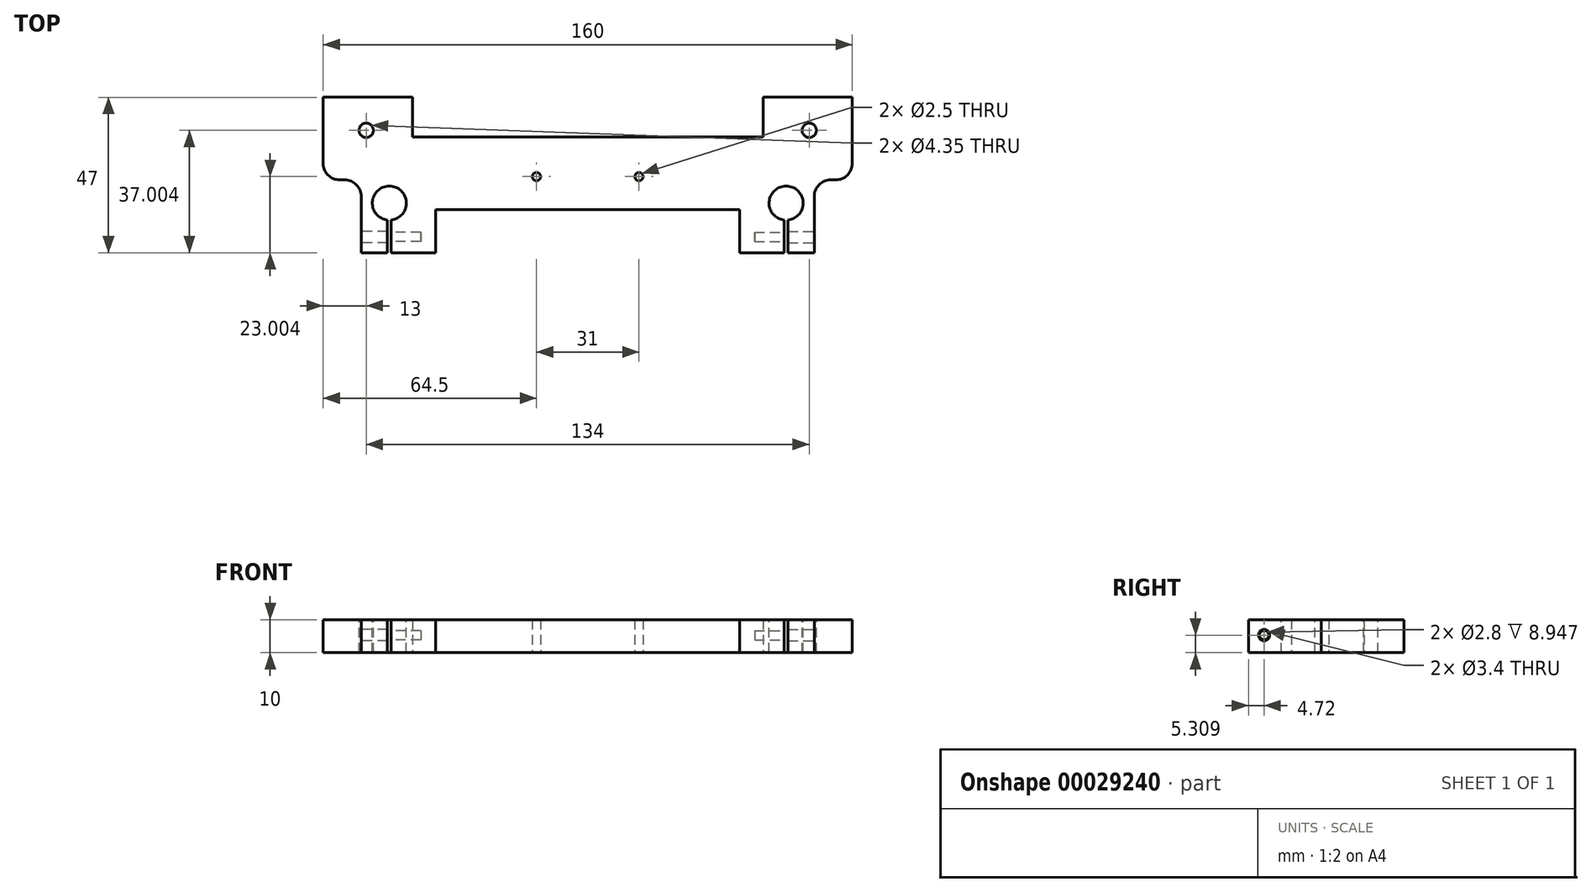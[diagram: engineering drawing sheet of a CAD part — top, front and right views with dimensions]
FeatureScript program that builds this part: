
annotation { "Feature Type Name" : "Feature", "Feature Type Description" : "" }
export const myFeature = defineFeature(function(context is Context, id is Id, definition is map)
    precondition{}
    {
        {
            var Q0;
            Q0=qCreatedBy(makeId("Top.planeOp"),FACE);
            var sketch = newSketch(context, id + "F0", { "sketchPlane" : qUnion([Q0])});
            skLineSegment(sketch, "E0", {"start": v(-68.5, -12.82) * mm, "end": v(-68.5, 9.18) * mm});
            skLineSegment(sketch, "E1", {"start": v(-68.5, 9.18) * mm, "end": v(-80, 9.18) * mm});
            skLineSegment(sketch, "E2", {"start": v(-80, 9.18) * mm, "end": v(-80, 34.18) * mm});
            skLineSegment(sketch, "E3", {"start": v(-80, 34.18) * mm, "end": v(-53, 34.18) * mm});
            skLineSegment(sketch, "E4", {"start": v(-53, 34.18) * mm, "end": v(-53, 22.18) * mm});
            skLineSegment(sketch, "E5", {"start": v(-53, 22.18) * mm, "end": v(0, 22.18) * mm});
            skLineSegment(sketch, "E6", {"start": v(-46, -12.82) * mm, "end": v(-46, 0.18) * mm});
            skLineSegment(sketch, "E7", {"start": v(-46, 0.18) * mm, "end": v(0, 0.18) * mm});
            skLineSegment(sketch, "E8", {"start": v(0, 22.18) * mm, "end": v(0, 0.18) * mm});
            skLineSegment(sketch, "E9", {"start": v(-68.5, -12.82) * mm, "end": v(-46, -12.82) * mm});
            skCircle(sketch, "E10", {"center": v(-15.5, 10.18) * mm, "radius": 1.25 * mm});
            skSolve(sketch);
        }
        {
            var Q0;
            Q0=qSketchRegion(id+"F0",true);
            extrude(context, id + "F1", {"entities" : qUnion([Q0]), "depth" : 10 * mm});
        }
        {
            var Q0;
            Q0=makeQuery(id+"F1.opExtrude","SWEPT_FACE",FACE,{"disambiguationData":[OSD([sQuery(id+"F0.wireOp",EDGE,"7c0e0c7f-b6a2-43cf-9337-3745fbf1bbcf")])]});
            var sketch = newSketch(context, id + "F2", { "sketchPlane" : qUnion([Q0])});
            skLineSegment(sketch, "E11", {"start": v(0, 5) * mm, "end": v(0, 5) * mm});
            skCircle(sketch, "E12", {"center": v(-15.5, 5) * mm, "radius": 1.6 * mm});
            skCircle(sketch, "E13", {"center": v(0, 20.5) * mm, "radius": 10.75 * mm});
            skSolve(sketch);
        }
        {
            var Q0;
            {var subQ0=makeQuery(id+"F1.opExtrude","CAP_FACE",FACE,{"disambiguationData":[OSD([sQuery(id+"F0.wireOp",EDGE,"7c0e0c7f-b6a2-43cf-9337-3745fbf1bbcf"),sQuery(id+"F0.wireOp",EDGE,"fd64a43a-5635-4f94-a977-4dd36923accb"),sQuery(id+"F0.wireOp",EDGE,"1334f7d4-4c90-4769-8fa3-fe5f576fb005"),sQuery(id+"F0.wireOp",EDGE,"E0"),sQuery(id+"F0.wireOp",EDGE,"E1"),sQuery(id+"F0.wireOp",EDGE,"E2"),sQuery(id+"F0.wireOp",EDGE,"E3"),sQuery(id+"F0.wireOp",EDGE,"E4"),sQuery(id+"F0.wireOp",EDGE,"E5"),sQuery(id+"F0.wireOp",EDGE,"a8eeaa19-4979-4e21-8f88-56795b57fb28")])],"isStart":false});Q0=makeQuery(id+"F10.boolean.opBoolean","MERGE",FACE,{"derivedFrom":[subQ0,makeQuery(id+"F10.opPattern","COPY",FACE,{"derivedFrom":subQ0,"instanceName":"1"})]});}
            var sketch = newSketch(context, id + "F3", { "sketchPlane" : qUnion([Q0])});
            skCircle(sketch, "E14", {"center": v(-60, 2.18) * mm, "radius": 5.15 * mm});
            skCircle(sketch, "E15", {"center": v(-67, 24.18) * mm, "radius": 2.17 * mm});
            skLineSegment(sketch, "E16", {"start": v(-60, 2.18) * mm, "end": v(-60, -13.1) * mm, "construction": true});
            skLineSegment(sketch, "E17.bottom", {"start": v(-60.55, -0.9) * mm, "end": v(-59.45, -0.9) * mm});
            skLineSegment(sketch, "E17.top", {"start": v(-60.55, -14.01) * mm, "end": v(-59.45, -14.01) * mm});
            skLineSegment(sketch, "E17.left", {"start": v(-60.55, -0.9) * mm, "end": v(-60.55, -14.01) * mm});
            skLineSegment(sketch, "E17.right", {"start": v(-59.45, -0.9) * mm, "end": v(-59.45, -14.01) * mm});
            skPoint(sketch, "E18", {"position": v(-60, -0.9) * mm});
            skSolve(sketch);
        }
        {
            var Q0;
            Q0=qSketchRegion(id+"F3",true);
            var Q1;
            {var subQ3=sQuery(id+"F3.wireOp",EDGE,"E17.bottom");Q1=makeQuery(id+"F3.imprint","IMPRINT",FACE,{"disambiguationData":[TD([[makeQuery(id+"F3.imprint","IMPRINT",EDGE,{"derivedFrom":subQ3}),-1.0]])]});}
            extrude(context, id + "F4", {"entities" : qUnion([Q0, Q1]), "operationType" : NewBodyOperationType.REMOVE, "endBound" : BoundingType.THROUGH_ALL, "oppositeDirection" : true, "depth" : 25 * mm});
        }
        {
            var Q0;
            Q0=makeQuery(id+"F1.opExtrude","SWEPT_EDGE",EDGE,{"disambiguationData":[OSD([sQuery(id+"F0.wireOp",EDGE,"E1"),sQuery(id+"F0.wireOp",EDGE,"E2")])]});
            fillet(context, id + "F5", {"entities" : qUnion([Q0]), "radius" : 5 * mm, "tangentPropagation" : true, "allowEdgeOverflow" : false});
        }
        {
            var Q0;
            Q0=makeQuery(id+"F1.opExtrude","SWEPT_EDGE",EDGE,{"disambiguationData":[OSD([sQuery(id+"F0.wireOp",EDGE,"E0"),sQuery(id+"F0.wireOp",EDGE,"E1")])]});
            fillet(context, id + "F6", {"entities" : qUnion([Q0]), "radius" : 5 * mm, "tangentPropagation" : true, "allowEdgeOverflow" : false});
        }
        {
            var Q0;
            Q0=makeQuery(id+"F1.opExtrude","SWEPT_FACE",FACE,{"disambiguationData":[OSD([sQuery(id+"F0.wireOp",EDGE,"E0")])]});
            var sketch = newSketch(context, id + "F7", { "sketchPlane" : qUnion([Q0])});
            skCircle(sketch, "E19", {"center": v(8.1, 5.3) * mm, "radius": 1.7 * mm});
            skCircle(sketch, "E20", {"center": v(8.1, 5.3) * mm, "radius": 1.4 * mm});
            skSolve(sketch);
        }
        {
            var Q0;
            Q0=makeQuery(id+"F7.imprint","IMPRINT",FACE,{"disambiguationData":[TD([[makeQuery(id+"F7.imprint","IMPRINT",EDGE,{"derivedFrom":sQuery(id+"F7.wireOp",EDGE,"E20")}),1.0]])]});
            extrude(context, id + "F8", {"entities" : qUnion([Q0]), "operationType" : NewBodyOperationType.REMOVE, "oppositeDirection" : true, "depth" : 18 * mm});
        }
        {
            var Q0;
            Q0=makeQuery(id+"F7.imprint","IMPRINT",FACE,{"disambiguationData":[TD([[makeQuery(id+"F7.imprint","IMPRINT",EDGE,{"derivedFrom":sQuery(id+"F7.wireOp",EDGE,"E20")}),1.0]])]});
            var Q1;
            Q1=makeQuery(id+"F7.imprint","IMPRINT",FACE,{"disambiguationData":[TD([[makeQuery(id+"F7.imprint","IMPRINT",EDGE,{"derivedFrom":sQuery(id+"F7.wireOp",EDGE,"E19")}),1.0]])]});
            extrude(context, id + "F9", {"entities" : qUnion([Q0, Q1]), "operationType" : NewBodyOperationType.REMOVE, "endBound" : BoundingType.UP_TO_NEXT, "oppositeDirection" : true, "depth" : 25 * mm});
        }
        {
            var Q0;
            Q0=makeQuery(id+"F1.opExtrude","SWEPT_BODY",BODY,{"disambiguationData":[OSD([sQuery(id+"F0.wireOp",EDGE,"7c0e0c7f-b6a2-43cf-9337-3745fbf1bbcf"),sQuery(id+"F0.wireOp",EDGE,"fd64a43a-5635-4f94-a977-4dd36923accb"),sQuery(id+"F0.wireOp",EDGE,"1334f7d4-4c90-4769-8fa3-fe5f576fb005"),sQuery(id+"F0.wireOp",EDGE,"E0"),sQuery(id+"F0.wireOp",EDGE,"E1"),sQuery(id+"F0.wireOp",EDGE,"E2"),sQuery(id+"F0.wireOp",EDGE,"E3"),sQuery(id+"F0.wireOp",EDGE,"E4"),sQuery(id+"F0.wireOp",EDGE,"E5"),sQuery(id+"F0.wireOp",EDGE,"a8eeaa19-4979-4e21-8f88-56795b57fb28")])]});
            var Q1;
            Q1=qCreatedBy(makeId("Right.planeOp"),FACE);
            mirror(context, id + "F10", {"operationType" : NewBodyOperationType.ADD, "entities" : qUnion([Q0]), "mirrorPlane" : qUnion([Q1])});
        }
    });
